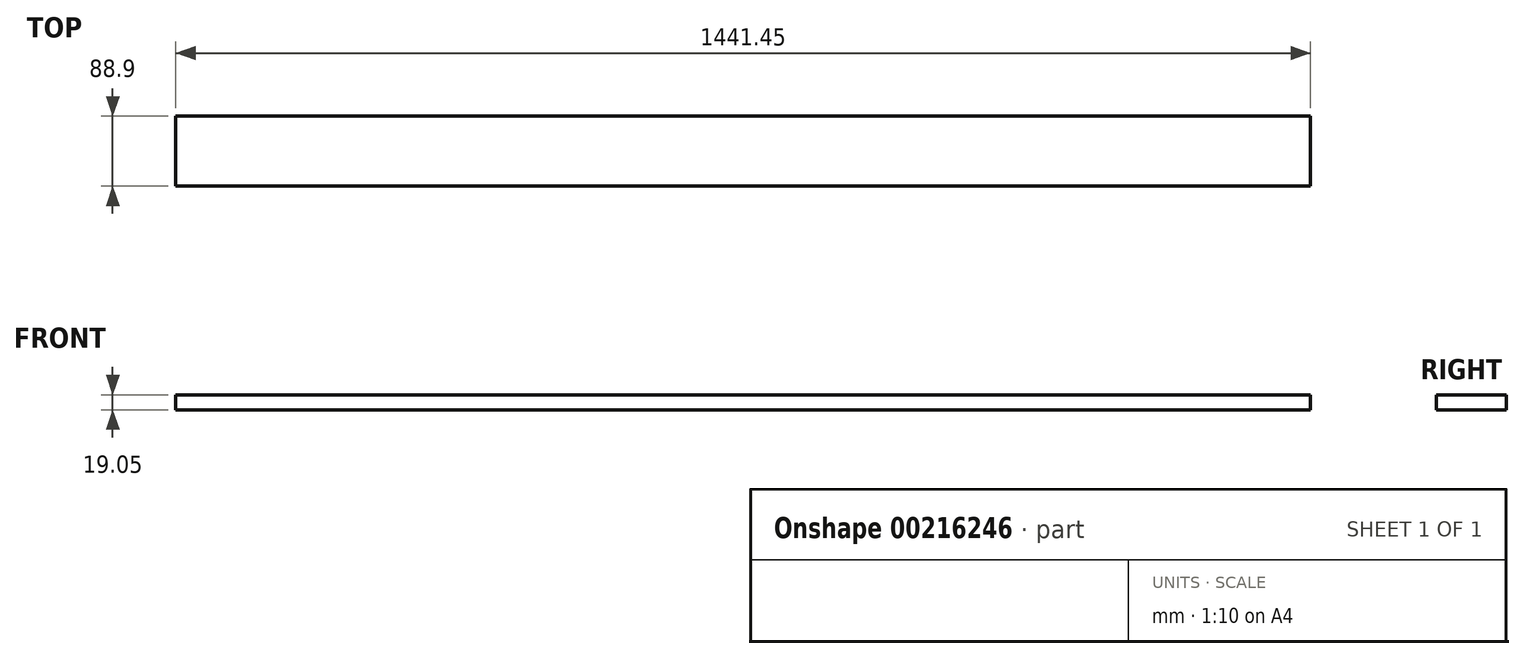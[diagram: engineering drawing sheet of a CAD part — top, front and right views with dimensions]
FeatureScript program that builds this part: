
annotation { "Feature Type Name" : "Feature", "Feature Type Description" : "" }
export const myFeature = defineFeature(function(context is Context, id is Id, definition is map)
    precondition{}
    {
        {
            var Q0;
            Q0=qCreatedBy(makeId("Top.planeOp"),FACE);
            var sketch = newSketch(context, id + "F0", { "sketchPlane" : qUnion([Q0])});
            skLineSegment(sketch, "E0", {"start": v(-5813.08, 341.69) * mm, "end": v(-4371.63, 341.69) * mm});
            skLineSegment(sketch, "E1", {"start": v(-4371.63, 341.69) * mm, "end": v(-4371.63, 430.59) * mm});
            skLineSegment(sketch, "E2", {"start": v(-4371.63, 430.59) * mm, "end": v(-5813.08, 430.59) * mm});
            skLineSegment(sketch, "E3", {"start": v(-5813.08, 430.59) * mm, "end": v(-5813.08, 341.69) * mm});
            skSolve(sketch);
        }
        {
            var Q0;
            Q0=makeQuery(id+"F0.imprint","IMPRINT",FACE,{"disambiguationData":[TD([[makeQuery(id+"F0.imprint","IMPRINT",EDGE,{"derivedFrom":sQuery(id+"F0.wireOp",EDGE,"E0")}),1.0]])]});
            extrude(context, id + "F1", {"entities" : qUnion([Q0]), "depth" : 19.05 * mm});
        }
    });
